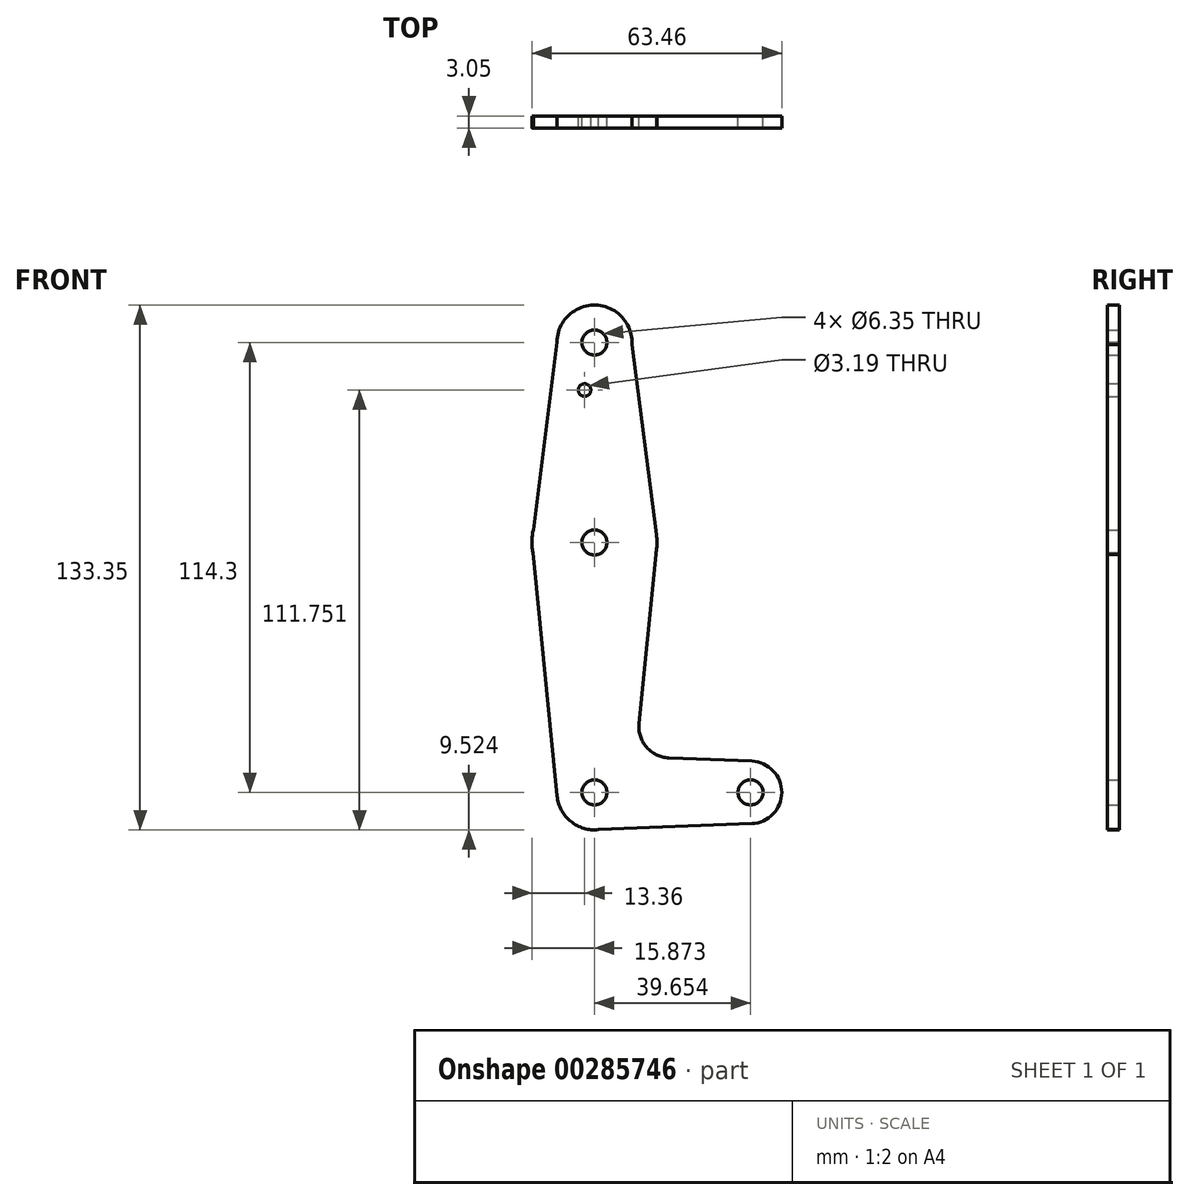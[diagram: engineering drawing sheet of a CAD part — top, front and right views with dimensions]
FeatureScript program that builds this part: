
annotation { "Feature Type Name" : "Feature", "Feature Type Description" : "" }
export const myFeature = defineFeature(function(context is Context, id is Id, definition is map)
    precondition{}
    {
        {
            var Q0;
            Q0=qCreatedBy(makeId("Front.planeOp"),FACE);
            var sketch = newSketch(context, id + "F0", { "sketchPlane" : qUnion([Q0])});
            skCircle(sketch, "E0", {"center": v(-47.03, 58.58) * mm, "radius": 9.53 * mm});
            skLineSegment(sketch, "E1", {"start": v(-47.03, 58.58) * mm, "end": v(-47.03, 7.78) * mm});
            skCircle(sketch, "E2", {"center": v(-47.03, 7.78) * mm, "radius": 15.88 * mm});
            skLineSegment(sketch, "E3", {"start": v(-47.03, 7.78) * mm, "end": v(-47.03, -55.72) * mm});
            skCircle(sketch, "E4", {"center": v(-47.03, -55.72) * mm, "radius": 9.53 * mm});
            skLineSegment(sketch, "E5", {"start": v(-47.03, -55.72) * mm, "end": v(-7.37, -55.72) * mm});
            skLineSegment(sketch, "E6.trimOffspring", {"start": v(-62.58, 10.99) * mm, "end": v(-62.58, 10.99) * mm});
            skLineSegment(sketch, "E7", {"start": v(-56.29, 60.8) * mm, "end": v(-62.58, 10.99) * mm});
            skLineSegment(sketch, "E8", {"start": v(-37.94, 61.44) * mm, "end": v(-31.28, 9.81) * mm});
            skLineSegment(sketch, "E9", {"start": v(-62.89, 7.14) * mm, "end": v(-56.5, -56.66) * mm});
            skLineSegment(sketch, "E10", {"start": v(-31.15, 7.72) * mm, "end": v(-35.72, -38.22) * mm});
            skCircle(sketch, "E11", {"center": v(-7.37, -55.72) * mm, "radius": 7.94 * mm});
            skLineSegment(sketch, "E12", {"start": v(-46, -65.18) * mm, "end": v(-7.06, -63.65) * mm});
            skCircle(sketch, "E13", {"center": v(-47.03, 58.58) * mm, "radius": 3.18 * mm});
            skCircle(sketch, "E14", {"center": v(-47.03, 7.78) * mm, "radius": 3.18 * mm});
            skCircle(sketch, "E15", {"center": v(-47.03, -55.72) * mm, "radius": 3.18 * mm});
            skCircle(sketch, "E16", {"center": v(-7.37, -55.72) * mm, "radius": 3.18 * mm});
            skCircle(sketch, "E17", {"center": v(-49.54, 46.51) * mm, "radius": 1.6 * mm});
            skLineSegment(sketch, "E18", {"start": v(-28.12, -46.95) * mm, "end": v(-7.06, -47.78) * mm});
            skArc(sketch, "E19.filletArc", {"start": v(-35.72, -38.22) * mm, "mid": v(-33.8, -44.22) * mm, "end": v(-28.12, -46.95) * mm});
            skSolve(sketch);
        }
        {
            var Q0;
            Q0 = qSketchRegion(id + "F0", true);
            var Q1;
            {var subQ0=sQuery(id+"F0.wireOp",EDGE,"E4");var subQ1=sQuery(id+"F0.wireOp",EDGE,"E3");var subQ2=makeQuery(id+"F0.imprint","INTERSECT",VERTEX,{"derivedFrom":[subQ1,subQ0]});Q1=makeQuery(id+"F0.imprint","IMPRINT",FACE,{"disambiguationData":[TD([[makeQuery(id+"F0.imprint","IMPRINT",EDGE,{"disambiguationData":[TD([[subQ2,-1.0]])],"derivedFrom":subQ1}),1.0]])]});}
            extrude(context, id + "F1", {"entities" : qUnion([Q0, Q1]), "depth" : 3.05 * mm});
        }
    });
